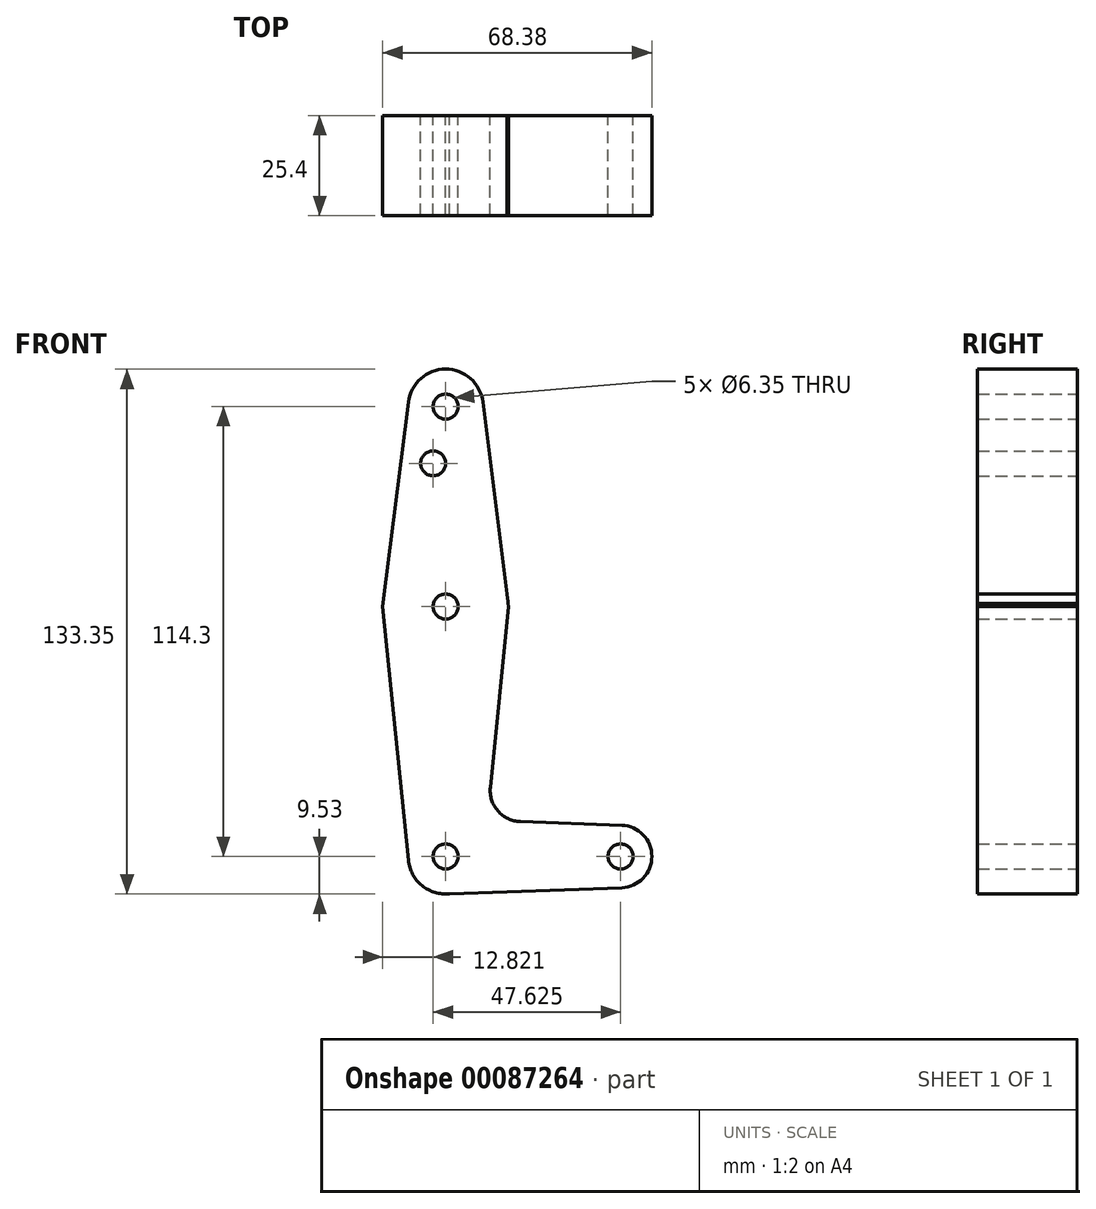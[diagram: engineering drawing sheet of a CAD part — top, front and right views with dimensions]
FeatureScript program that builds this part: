
annotation { "Feature Type Name" : "Feature", "Feature Type Description" : "" }
export const myFeature = defineFeature(function(context is Context, id is Id, definition is map)
    precondition{}
    {
        {
            var Q0;
            Q0=qCreatedBy(makeId("Front.planeOp"),FACE);
            var sketch = newSketch(context, id + "F0", { "sketchPlane" : qUnion([Q0])});
            skLineSegment(sketch, "E0", {"start": v(-20.3, 50.8) * mm, "end": v(-20.3, -63.5) * mm});
            skLineSegment(sketch, "E1", {"start": v(-20.3, -63.5) * mm, "end": v(24.15, -63.5) * mm});
            skCircle(sketch, "E2", {"center": v(-20.3, 50.8) * mm, "radius": 9.52 * mm});
            skCircle(sketch, "E3", {"center": v(-20.3, -63.5) * mm, "radius": 9.53 * mm});
            skCircle(sketch, "E4", {"center": v(24.15, -63.5) * mm, "radius": 7.94 * mm});
            skCircle(sketch, "E5", {"center": v(-20.3, 0) * mm, "radius": 15.88 * mm});
            skLineSegment(sketch, "E6", {"start": v(-29.75, 52) * mm, "end": v(-36.3, 0) * mm});
            skLineSegment(sketch, "E7", {"start": v(-10.85, 52) * mm, "end": v(-4.35, 0) * mm});
            skLineSegment(sketch, "E8", {"start": v(-36.3, 0) * mm, "end": v(-29.78, -64.46) * mm});
            skLineSegment(sketch, "E9", {"start": v(-4.35, 0) * mm, "end": v(-8.96, -45.9) * mm});
            skLineSegment(sketch, "E10", {"start": v(-1.34, -54.65) * mm, "end": v(24.43, -55.57) * mm});
            skLineSegment(sketch, "E11", {"start": v(-20.62, -73.02) * mm, "end": v(24.43, -71.43) * mm});
            skCircle(sketch, "E12", {"center": v(-20.3, 50.8) * mm, "radius": 3.18 * mm});
            skCircle(sketch, "E13", {"center": v(-20.3, 0) * mm, "radius": 3.18 * mm});
            skCircle(sketch, "E14", {"center": v(-20.3, -63.5) * mm, "radius": 3.18 * mm});
            skCircle(sketch, "E15", {"center": v(24.15, -63.5) * mm, "radius": 3.18 * mm});
            skArc(sketch, "E16.filletArc", {"start": v(-8.96, -45.9) * mm, "mid": v(-7.04, -51.93) * mm, "end": v(-1.34, -54.65) * mm});
            skCircle(sketch, "E17", {"center": v(-23.48, 36.39) * mm, "radius": 3.18 * mm});
            skSolve(sketch);
        }
        {
            var Q0;
            Q0 = qSketchRegion(id + "F0", true);
            var Q1;
            {var subQ0=sQuery(id+"F0.wireOp",EDGE,"E3");var subQ1=sQuery(id+"F0.wireOp",EDGE,"E0");var subQ2=makeQuery(id+"F0.imprint","INTERSECT",VERTEX,{"derivedFrom":[subQ1,subQ0]});Q1=makeQuery(id+"F0.imprint","IMPRINT",FACE,{"disambiguationData":[TD([[makeQuery(id+"F0.imprint","IMPRINT",EDGE,{"disambiguationData":[TD([[subQ2,-1.0]])],"derivedFrom":subQ1}),1.0]])]});}
            extrude(context, id + "F1", {"entities" : qUnion([Q0, Q1]), "depth" : 25.4 * mm});
        }
    });
